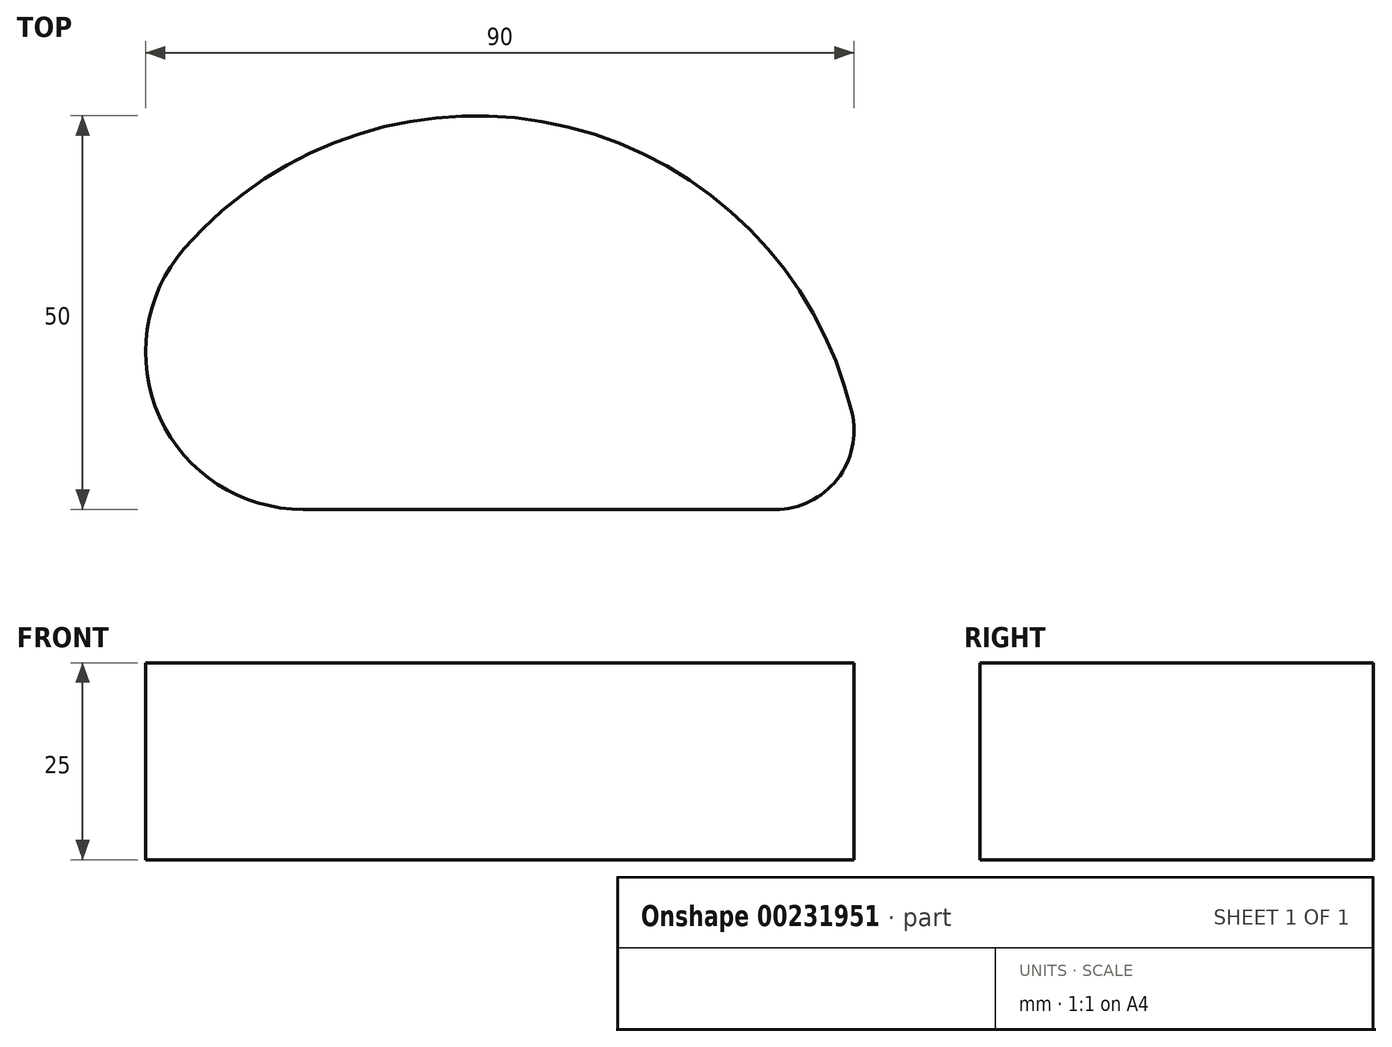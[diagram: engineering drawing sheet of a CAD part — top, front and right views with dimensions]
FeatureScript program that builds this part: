
annotation { "Feature Type Name" : "Feature", "Feature Type Description" : "" }
export const myFeature = defineFeature(function(context is Context, id is Id, definition is map)
    precondition{}
    {
        {
            var Q0;
            Q0=qCreatedBy(makeId("Top.planeOp"),FACE);
            var sketch = newSketch(context, id + "F0", { "sketchPlane" : qUnion([Q0])});
            skLineSegment(sketch, "E0", {"start": v(0, 0) * mm, "end": v(-60, 0) * mm});
            skArc(sketch, "E1", {"start": v(-60, 0) * mm, "mid": v(-78.2, 11.71) * mm, "end": v(-75.09, 33.13) * mm});
            skArc(sketch, "E2", {"start": v(-75.09, 33.13) * mm, "mid": v(-26.34, 48.59) * mm, "end": v(9.72, 12.33) * mm});
            skArc(sketch, "E3", {"start": v(9.72, 12.33) * mm, "mid": v(7.85, 3.8) * mm, "end": v(0, 0) * mm});
            skLineSegment(sketch, "E4", {"start": v(-80, 47.23) * mm, "end": v(-80, -14.3) * mm, "construction": true});
            skLineSegment(sketch, "E5", {"start": v(10, 43.54) * mm, "end": v(10, -20.26) * mm, "construction": true});
            skSolve(sketch);
        }
        {
            var Q0;
            Q0=makeQuery(id+"F0.imprint","IMPRINT",FACE,{"disambiguationData":[TD([[makeQuery(id+"F0.imprint","IMPRINT",EDGE,{"derivedFrom":sQuery(id+"F0.wireOp",EDGE,"E0")}),-1.0]])]});
            extrude(context, id + "F1", {"entities" : qUnion([Q0]), "depth" : 25 * mm});
        }
    });
